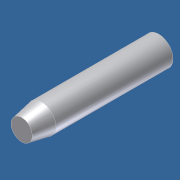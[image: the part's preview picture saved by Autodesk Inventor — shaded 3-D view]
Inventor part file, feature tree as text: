
AUTODESK INVENTOR PART (.ipt)
format: ipt  version: 2012 (Build 160160000, 160)  size: 78,336 bytes
history: native  units: in
note: dims shown in document units (in); Inventor stores cm internally (conversion verified against a paired STEP export)
features: extrude x1, chamfer x1, sketch x1
ambient origin geometry x8: Origin, YZ Plane, XZ Plane, XY Plane, X Axis, Y Axis, Z Axis, Center Point
bodies: Solid1 (feature_tree)
feature tree (3):
  extrude  "Extrusion1"  Depth=6.875in TaperAngle=0.0deg
  chamfer  "Chamfer1"  Distance=1.0in Angle=45.0deg
  sketch  "Sketch1"  dims[d0=1.4375in d1=6.875in d2=0.0in d3=1.0in d4=0.1875in d5=45.0deg]
